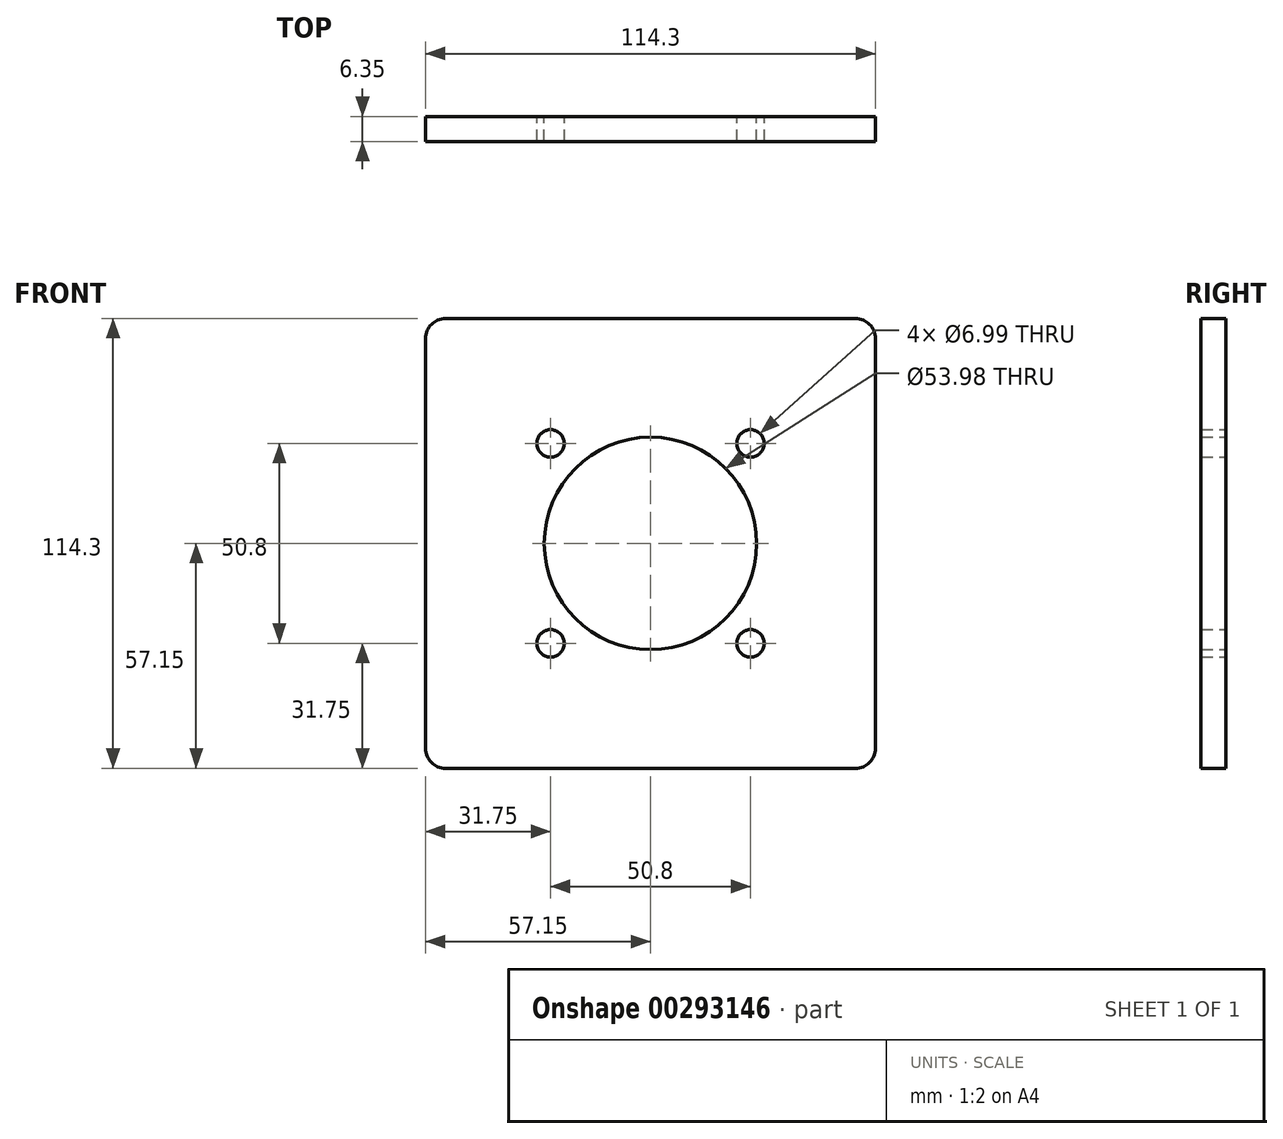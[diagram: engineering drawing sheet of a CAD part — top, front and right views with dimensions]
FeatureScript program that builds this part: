
annotation { "Feature Type Name" : "Feature", "Feature Type Description" : "" }
export const myFeature = defineFeature(function(context is Context, id is Id, definition is map)
    precondition{}
    {
        {
            var Q0;
            Q0=qCreatedBy(makeId("Front.planeOp"),FACE);
            var sketch = newSketch(context, id + "F0", { "sketchPlane" : qUnion([Q0])});
            skLineSegment(sketch, "E0.bottom", {"start": v(5.08, 0) * mm, "end": v(109.22, 0) * mm});
            skLineSegment(sketch, "E0.top", {"start": v(5.08, 114.3) * mm, "end": v(109.22, 114.3) * mm});
            skLineSegment(sketch, "E0.left", {"start": v(0, 5.08) * mm, "end": v(0, 109.22) * mm});
            skLineSegment(sketch, "E0.right", {"start": v(114.3, 5.08) * mm, "end": v(114.3, 109.22) * mm});
            skPoint(sketch, "E1.visualSharp", {"position": v(0, 0) * mm});
            skArc(sketch, "E1.filletArc", {"start": v(0, 5.08) * mm, "mid": v(1.49, 1.49) * mm, "end": v(5.08, 0) * mm});
            skPoint(sketch, "E2.visualSharp", {"position": v(0, 114.3) * mm});
            skArc(sketch, "E2.filletArc", {"start": v(5.08, 114.3) * mm, "mid": v(1.49, 112.81) * mm, "end": v(0, 109.22) * mm});
            skPoint(sketch, "E3.visualSharp", {"position": v(114.3, 114.3) * mm});
            skArc(sketch, "E3.filletArc", {"start": v(114.3, 109.22) * mm, "mid": v(112.81, 112.81) * mm, "end": v(109.22, 114.3) * mm});
            skPoint(sketch, "E4.visualSharp", {"position": v(114.3, 0) * mm});
            skArc(sketch, "E4.filletArc", {"start": v(109.22, 0) * mm, "mid": v(112.81, 1.49) * mm, "end": v(114.3, 5.08) * mm});
            skCircle(sketch, "E5", {"center": v(57.15, 57.15) * mm, "radius": 26.99 * mm});
            skPoint(sketch, "E5.centerSnap0", {"position": v(0, 57.15) * mm});
            skPoint(sketch, "E5.centerSnap1", {"position": v(57.15, 0) * mm});
            skCircle(sketch, "E6", {"center": v(31.75, 31.75) * mm, "radius": 3.5 * mm});
            skCircle(sketch, "E7.0.1.0", {"center": v(31.75, 82.55) * mm, "radius": 3.5 * mm});
            skCircle(sketch, "E7.1.0.0", {"center": v(82.55, 31.75) * mm, "radius": 3.5 * mm});
            skCircle(sketch, "E7.1.1.0", {"center": v(82.55, 82.55) * mm, "radius": 3.5 * mm});
            skLineSegment(sketch, "E7.direction1", {"start": v(31.75, 31.75) * mm, "end": v(82.55, 31.75) * mm, "construction": true});
            skLineSegment(sketch, "E7.direction2", {"start": v(31.75, 31.75) * mm, "end": v(31.75, 82.55) * mm, "construction": true});
            skSolve(sketch);
        }
        {
            var Q0;
            Q0=makeQuery(id+"F0.imprint","IMPRINT",FACE,{"disambiguationData":[TD([[makeQuery(id+"F0.imprint","IMPRINT",EDGE,{"derivedFrom":sQuery(id+"F0.wireOp",EDGE,"E0.bottom")}),1.0]])]});
            extrude(context, id + "F1", {"entities" : qUnion([Q0]), "depth" : 6.35 * mm});
        }
    });
